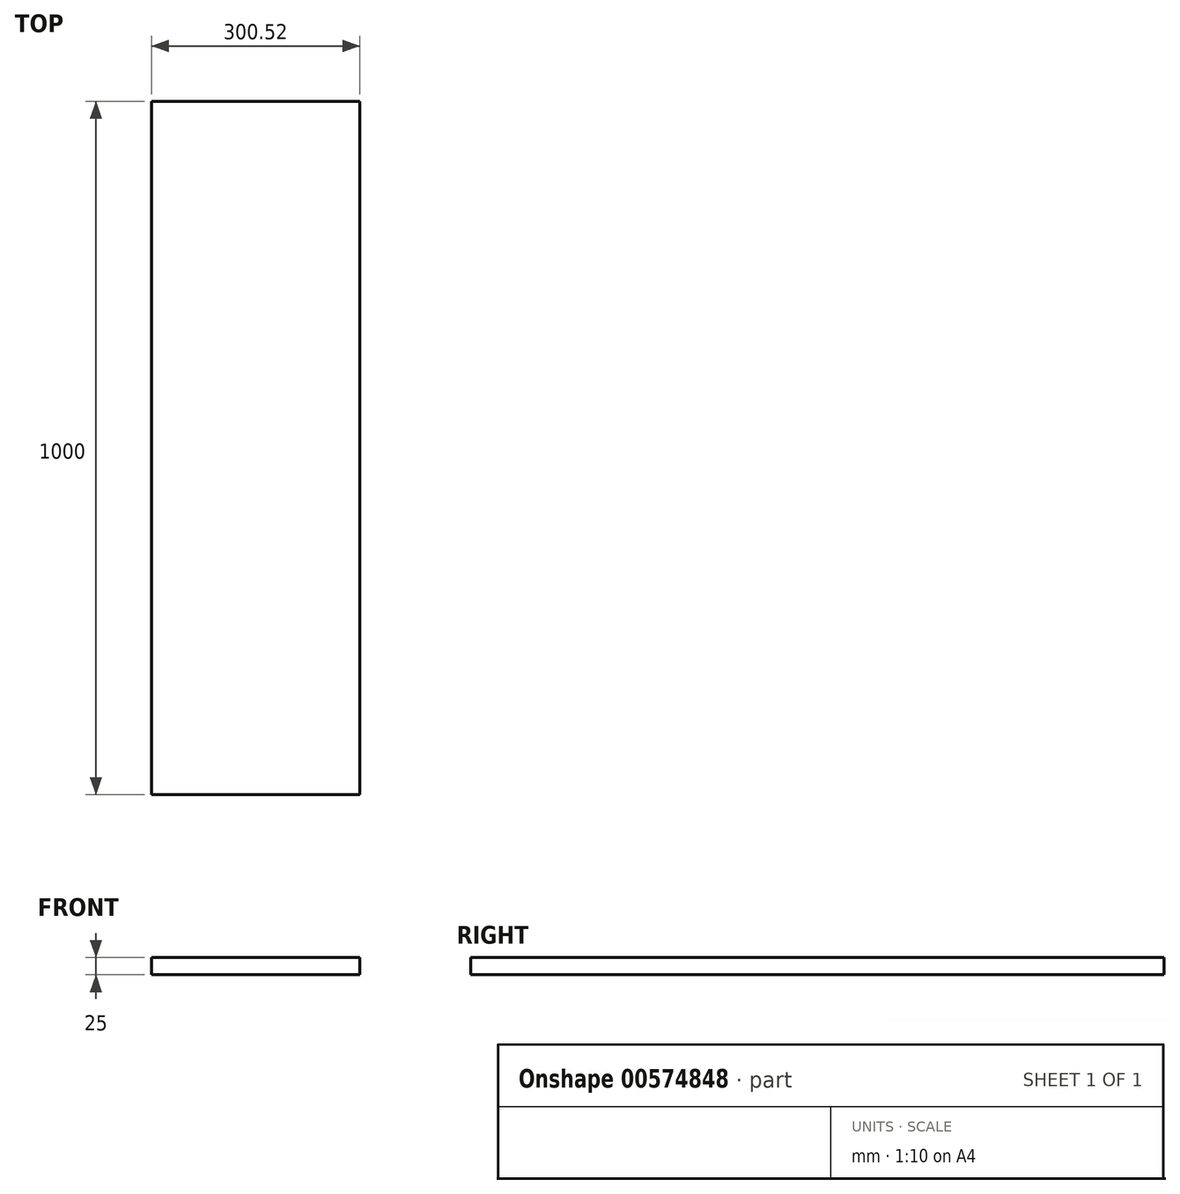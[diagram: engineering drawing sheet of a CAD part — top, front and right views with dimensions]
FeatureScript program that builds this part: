
annotation { "Feature Type Name" : "Feature", "Feature Type Description" : "" }
export const myFeature = defineFeature(function(context is Context, id is Id, definition is map)
    precondition{}
    {
        {
            var Q0;
            Q0=qCreatedBy(makeId("Top.planeOp"),FACE);
            var sketch = newSketch(context, id + "F0", { "sketchPlane" : qUnion([Q0])});
            skLineSegment(sketch, "E0.bottom", {"start": v(-150.26, -500) * mm, "end": v(150.26, -500) * mm});
            skLineSegment(sketch, "E0.top", {"start": v(-150.26, 500) * mm, "end": v(150.26, 500) * mm});
            skLineSegment(sketch, "E0.left", {"start": v(-150.26, -500) * mm, "end": v(-150.26, 500) * mm});
            skLineSegment(sketch, "E0.right", {"start": v(150.26, -500) * mm, "end": v(150.26, 500) * mm});
            skPoint(sketch, "E0.middle", {"position": v(0, 0) * mm});
            skSolve(sketch);
        }
        {
            var Q0;
            Q0=makeQuery(id+"F0.imprint","IMPRINT",FACE,{"disambiguationData":[TD([[makeQuery(id+"F0.imprint","IMPRINT",EDGE,{"derivedFrom":sQuery(id+"F0.wireOp",EDGE,"E0.bottom")}),1.0]])]});
            extrude(context, id + "F1", {"entities" : qUnion([Q0]), "depth" : 25 * mm, "offsetDistance" : 25 * mm});
        }
    });
